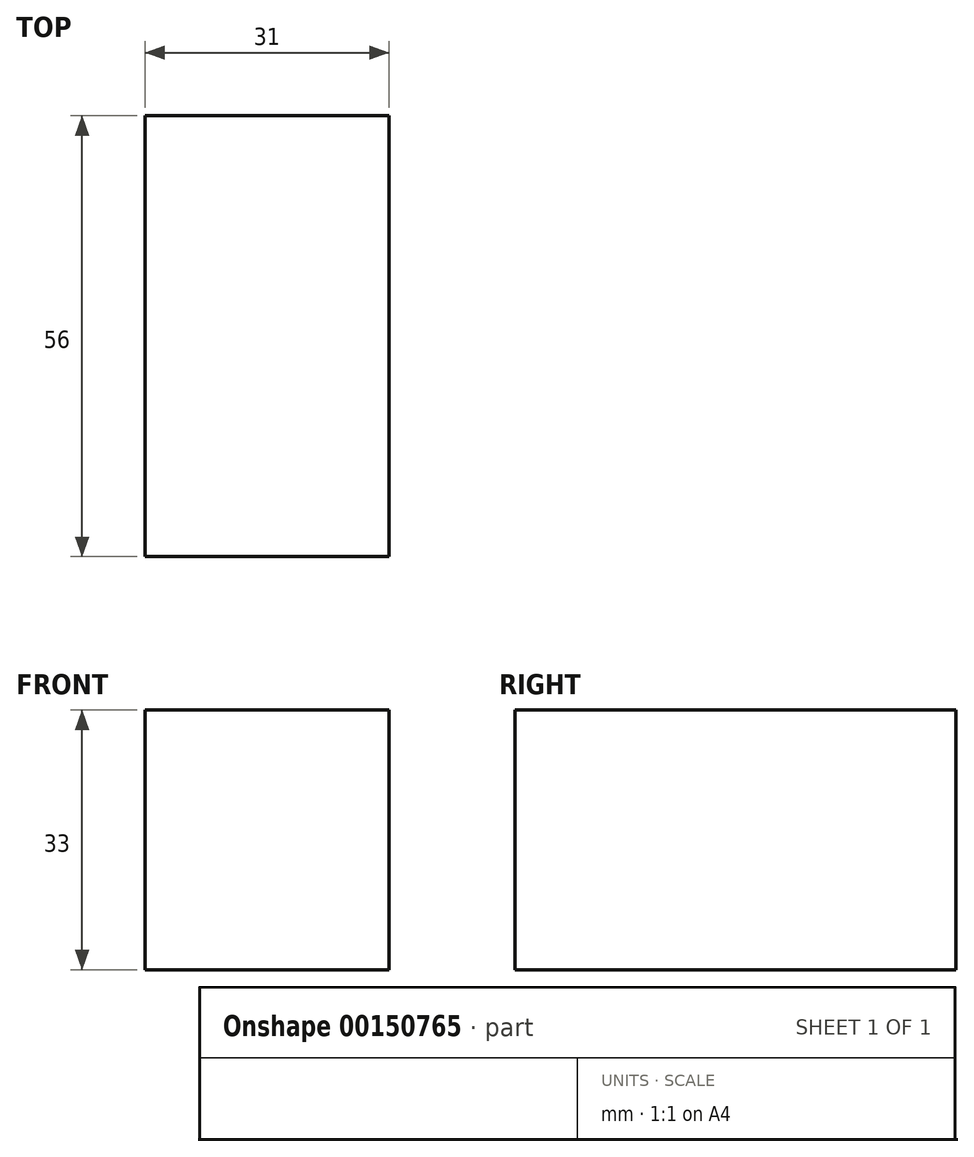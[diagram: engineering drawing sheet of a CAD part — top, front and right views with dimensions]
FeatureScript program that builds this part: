
annotation { "Feature Type Name" : "Feature", "Feature Type Description" : "" }
export const myFeature = defineFeature(function(context is Context, id is Id, definition is map)
    precondition{}
    {
        {
            var Q0;
            Q0=qCreatedBy(makeId("Top.planeOp"),FACE);
            var sketch = newSketch(context, id + "F0", { "sketchPlane" : qUnion([Q0])});
            skLineSegment(sketch, "E0.bottom", {"start": v(15.5, -28) * mm, "end": v(-15.5, -28) * mm});
            skLineSegment(sketch, "E0.top", {"start": v(15.5, 28) * mm, "end": v(-15.5, 28) * mm});
            skLineSegment(sketch, "E0.left", {"start": v(15.5, -28) * mm, "end": v(15.5, 28) * mm});
            skLineSegment(sketch, "E0.right", {"start": v(-15.5, -28) * mm, "end": v(-15.5, 28) * mm});
            skPoint(sketch, "E0.middle", {"position": v(0, 0) * mm});
            skSolve(sketch);
        }
        {
            var Q0;
            Q0 = qSketchRegion(id + "F0", true);
            extrude(context, id + "F1", {"entities" : qUnion([Q0]), "depth" : 33 * mm});
        }
    });
